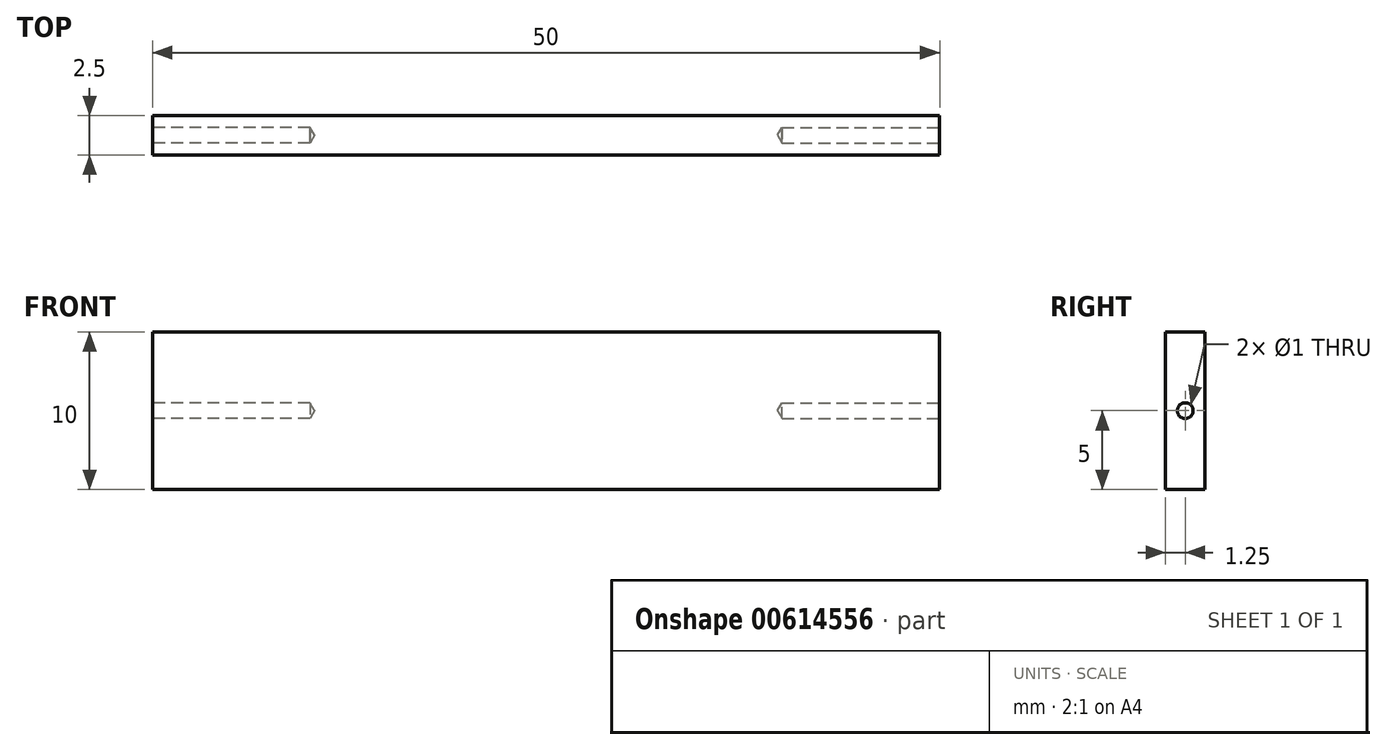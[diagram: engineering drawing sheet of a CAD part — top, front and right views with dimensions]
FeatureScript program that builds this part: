
annotation { "Feature Type Name" : "Feature", "Feature Type Description" : "" }
export const myFeature = defineFeature(function(context is Context, id is Id, definition is map)
    precondition{}
    {
        {
            var Q0;
            Q0=qCreatedBy(makeId("Front.planeOp"),FACE);
            var sketch = newSketch(context, id + "F0", { "sketchPlane" : qUnion([Q0])});
            skLineSegment(sketch, "E0.bottom", {"start": v(-15.14, 28.48) * mm, "end": v(34.86, 28.48) * mm});
            skLineSegment(sketch, "E0.top", {"start": v(-15.14, 18.48) * mm, "end": v(34.86, 18.48) * mm});
            skLineSegment(sketch, "E0.left", {"start": v(-15.14, 28.48) * mm, "end": v(-15.14, 18.48) * mm});
            skLineSegment(sketch, "E0.right", {"start": v(34.86, 28.48) * mm, "end": v(34.86, 18.48) * mm});
            skSolve(sketch);
        }
        {
            var Q0;
            Q0=makeQuery(id+"F0.imprint","IMPRINT",FACE,{"disambiguationData":[TD([[makeQuery(id+"F0.imprint","IMPRINT",EDGE,{"derivedFrom":sQuery(id+"F0.wireOp",EDGE,"E0.bottom")}),-1.0]])]});
            extrude(context, id + "F1", {"entities" : qUnion([Q0]), "endBound" : BoundingType.SYMMETRIC, "depth" : 2.5 * mm, "offsetDistance" : 25 * mm});
        }
        {
            var Q0;
            Q0=makeQuery(id+"F1.opExtrude","SWEPT_FACE",FACE,{"disambiguationData":[OSD([sQuery(id+"F0.wireOp",EDGE,"E0.left")])]});
            var sketch = newSketch(context, id + "F2", { "sketchPlane" : qUnion([Q0])});
            skLineSegment(sketch, "E1", {"start": v(0, 18.48) * mm, "end": v(0, 28.48) * mm});
            skLineSegment(sketch, "E2", {"start": v(0, 28.48) * mm, "end": v(0, 23.48) * mm});
            skSolve(sketch);
        }
        {
            var Q0;
            Q0=makeQuery(id+"F1.opExtrude","SWEPT_FACE",FACE,{"disambiguationData":[OSD([sQuery(id+"F0.wireOp",EDGE,"E0.right")])]});
            var sketch = newSketch(context, id + "F3", { "sketchPlane" : qUnion([Q0])});
            skLineSegment(sketch, "E3", {"start": v(0, 28.48) * mm, "end": v(0, 18.48) * mm});
            skLineSegment(sketch, "E4", {"start": v(0, 18.48) * mm, "end": v(0, 23.48) * mm});
            skSolve(sketch);
        }
        {
            var Q0;
            Q0=sQuery(id+"F3.wireOp",VERTEX,"E4.end");
            var Q1;
            Q1=makeQuery(id+"F1.opExtrude","SWEPT_BODY",BODY,{"disambiguationData":[OSD([sQuery(id+"F0.wireOp",EDGE,"E0.bottom"),sQuery(id+"F0.wireOp",EDGE,"E0.top"),sQuery(id+"F0.wireOp",EDGE,"E0.left"),sQuery(id+"F0.wireOp",EDGE,"E0.right")])]});
            hole(context, id + "F4", {"style" : HoleStyle.SIMPLE, "endStyle" : HoleEndStyle.BLIND, "holeDiameter" : 1 * mm, "majorDiameter" : 5 * mm, "holeDepth" : 10 * mm, "isTappedThrough" : true, "tappedDepth" : 12 * mm, "tapClearance" : 3, "locations" : qUnion([Q0]), "scope" : qUnion([Q1])});
        }
        {
            var Q0;
            Q0=sQuery(id+"F2.wireOp",VERTEX,"E2.end");
            var Q1;
            Q1=makeQuery(id+"F1.opExtrude","SWEPT_BODY",BODY,{"disambiguationData":[OSD([sQuery(id+"F0.wireOp",EDGE,"E0.bottom"),sQuery(id+"F0.wireOp",EDGE,"E0.top"),sQuery(id+"F0.wireOp",EDGE,"E0.left"),sQuery(id+"F0.wireOp",EDGE,"E0.right")])]});
            hole(context, id + "F5", {"style" : HoleStyle.SIMPLE, "endStyle" : HoleEndStyle.BLIND, "holeDiameter" : 1 * mm, "majorDiameter" : 5 * mm, "holeDepth" : 10 * mm, "isTappedThrough" : true, "tappedDepth" : 12 * mm, "tapClearance" : 3, "locations" : qUnion([Q0]), "scope" : qUnion([Q1])});
        }
    });
